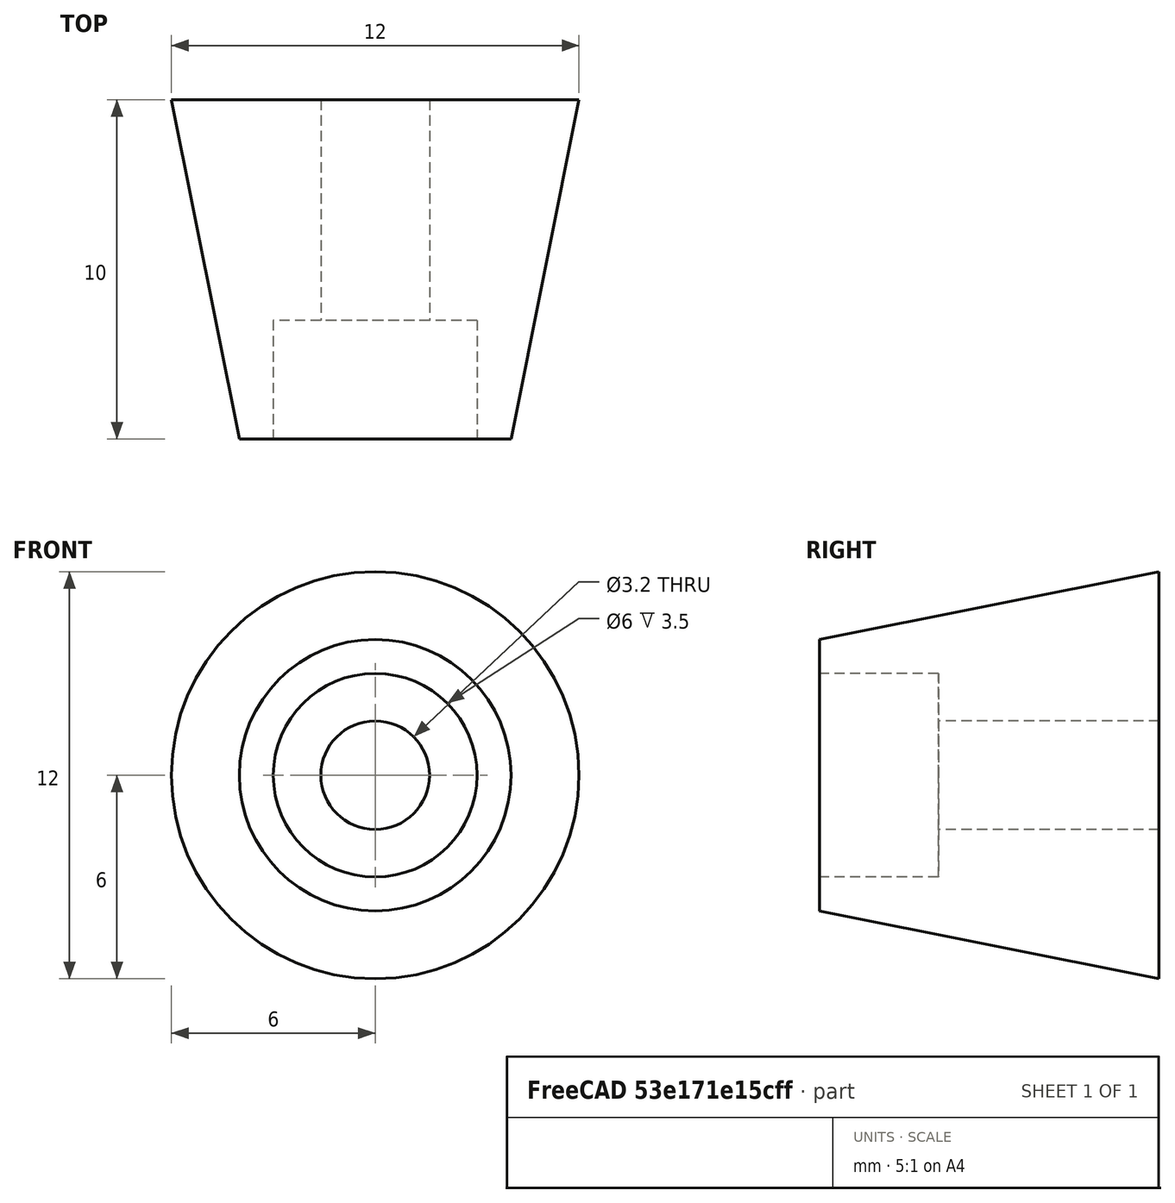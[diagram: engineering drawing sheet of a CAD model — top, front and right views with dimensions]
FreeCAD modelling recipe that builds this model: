
FCSTD DOCUMENT  (FreeCAD 0.19R21280 (Git))
Label: feet
License: All rights reserved
LicenseURL: http://en.wikipedia.org/wiki/All_rights_reserved
objects: Sketcher::SketchObject×1, PartDesign::Revolution×1, PartDesign::Body×1
note: 4 computed .brp shape members not serialized (recipe doc carries the construction recipe); baked Part::Feature solids carry a one-line shape summary decoded from their .brp

FEATURE [Sketcher::SketchObject] Sketch
  MapMode = 5
  Support = -> [XY_Plane]
  sketch-geometry (6):
    g0: LineSegment StartX=1.6 StartY=10 StartZ=0 EndX=1.6 EndY=3.5 EndZ=0
    g1: LineSegment StartX=1.6 StartY=3.5 StartZ=0 EndX=3 EndY=3.5 EndZ=0
    g2: LineSegment StartX=3 StartY=3.5 StartZ=0 EndX=3 EndY=0 EndZ=0
    g3: LineSegment StartX=3 StartY=0 StartZ=0 EndX=4 EndY=0 EndZ=0
    g4: LineSegment StartX=4 StartY=0 StartZ=0 EndX=6 EndY=10 EndZ=0
    g5: LineSegment StartX=1.6 StartY=10 StartZ=0 EndX=6 EndY=10 EndZ=0
  constraints (18):
    c: Vertical(g0)
    c: Coincident(g1,g0)
    c: Horizontal(g1)
    c: Coincident(g2,g1)
    c: PointOnObject(g2,g-1)
    c: Coincident(g3,g2)
    c: PointOnObject(g3,g-1)
    c: Coincident(g4,g3)
    c: Coincident(g5,g0)
    c: Coincident(g5,g4)
    c: Horizontal(g5)
    c: DistanceX(g-1,g0) = 1.6
    c: Vertical(g2)
    c: DistanceX(g-1,g2) = 3
    c: DistanceY(g-1,g4) = 10
    c: DistanceX(g-1,g3) = 4
    c: DistanceX(g-1,g4) = 6
    c: DistanceY(g2,g2) = 3.5
FEATURE [PartDesign::Revolution] Revolution
  Angle = 360
  Axis = (0,1,0)
  Base = (0,0,0)
  Profile = -> Sketch
  ReferenceAxis = -> Sketch [V_Axis]
  Reversed = true
FEATURE [PartDesign::Body] Body
  Group = -> [Sketch,Revolution]
  Origin = -> Origin
  Tip = -> Revolution
